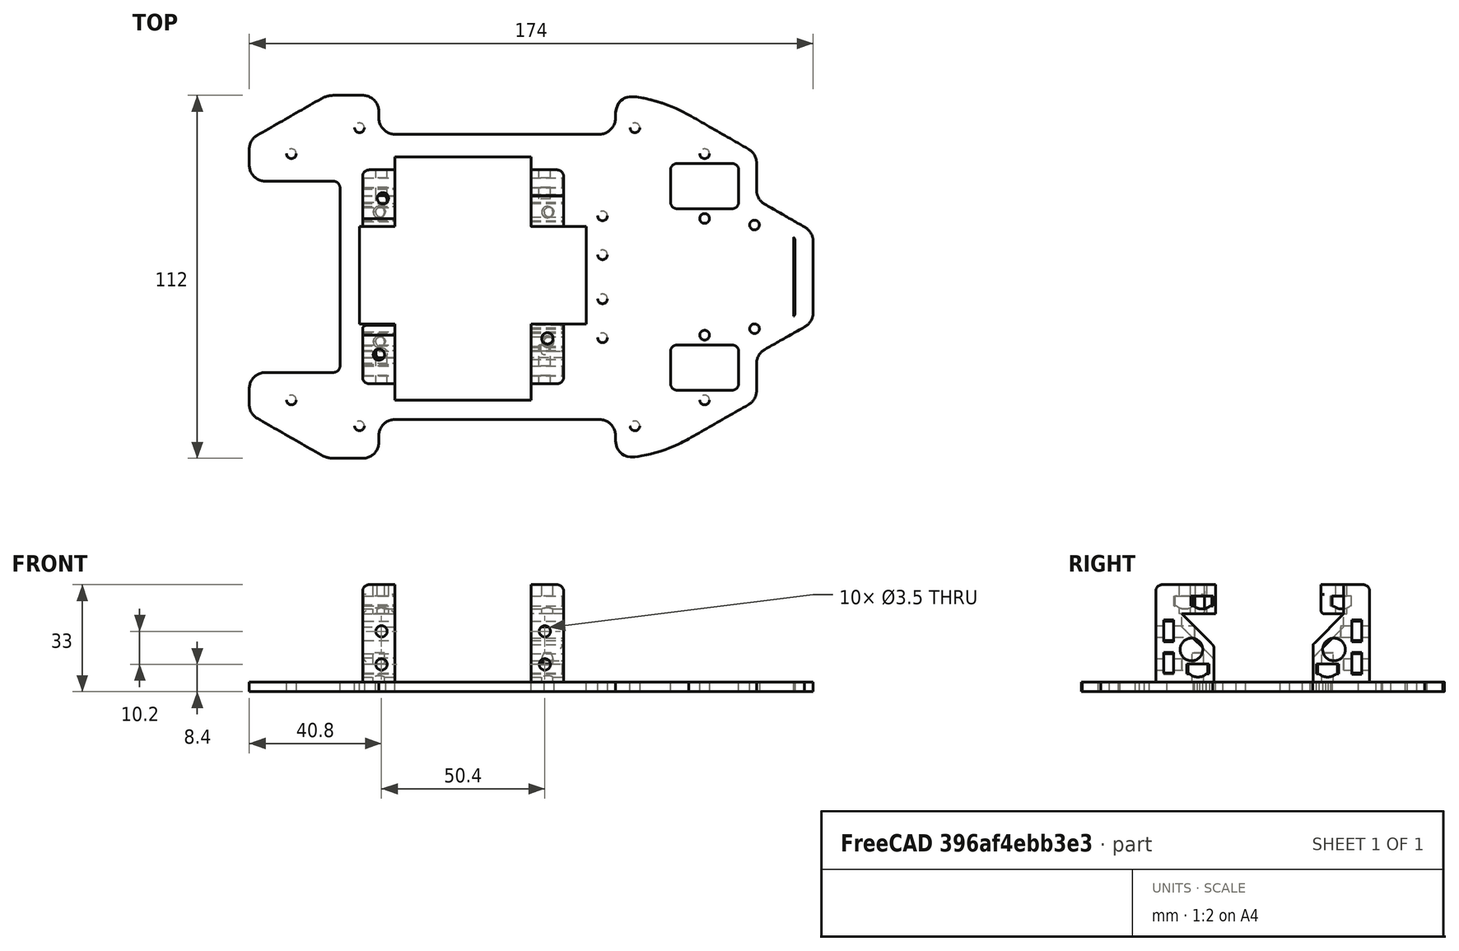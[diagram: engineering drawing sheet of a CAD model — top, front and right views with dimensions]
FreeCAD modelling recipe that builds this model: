
FCSTD DOCUMENT  (FreeCAD 0.16R6692 (Git))
Label: Base y cuerpo cortados
License: All rights reserved
LicenseURL: http://es.wikipedia.org/wiki/Todos_los_derechos_reservados
objects: Part::Box×7, Part::Cut×6, Part::Feature×2, Part::Fillet×1, Part::Chamfer×1, Part::MultiFuse×1, Part::FeaturePython×1
note: 19 computed .brp shape members not serialized (recipe doc carries the construction recipe); baked Part::Feature solids carry a one-line shape summary decoded from their .brp

FEATURE [Part::Feature] Cut048016001  label="Cut048017"
  shape: bbox 62 x 66 x 30 mm, 214 faces (baked)
FEATURE [Part::Fillet] Fillet  label="Redondeo_cuerpo"
  Base = -> Cut048016001
  Edges = 35 edges: [Edge159 r=1,Edge162 r=2,Edge164 r=2,Edge166 r=2,Edge169 r=2,Edge170 r=2,Edge171 r=2,Edge172 r=1,Edge173 r=1,Edge174 r=1,Edge175 r=1,Edge180 r=2,Edge183 r=2,Edge191 r=1,Edge192 r=1,Edge193 r=1,Edge195 r=1,Edge197 r=1,Edge204 r=1,Edge206 r=1,Edge272 r=1,Edge273 r=1,Edge274 r=1,Edge275 r=1,Edge276 r=1,Edge294 r=1,Edge295 r=1,Edge391 r=2,Edge393 r=1,Edge397 r=2,Edge403 r=1,Edge523 r=2,Edge525 r=1,Edge549 r=2,Edge550 r=1]
FEATURE [Part::Chamfer] Chamfer009  label="CUERPO_FINAL"
  Base = -> Fillet
  Edges = 30 edges r=0.4: [Edge70,Edge72,Edge74,Edge79,Edge89,Edge92,Edge96,Edge99,Edge101,Edge102,Edge104,Edge106,Edge108,Edge110,Edge112,Edge419,Edge421,Edge424,Edge426,Edge430,Edge432,Edge436,Edge438,Edge441,Edge443,Edge444,Edge446,Edge448,Edge450,Edge455]
FEATURE [Part::Feature] Part__Feature210  label="BASE_FINAL"
  shape: bbox 217.5 x 140 x 48.35 mm, 110 faces (baked)
FEATURE [Part::Box] Box  label="Cubo Y corte base"
  Height = 46
  Length = 42
  Placement = pos=(-12,-38,0) rot=(0,0,1;0rad)
  Width = 75
FEATURE [Part::Box] Box003  label="Cubo X corte cuerpo"
  Height = 49
  Length = 70
  Placement = pos=(-23,-14.5,0) rot=(0,0,1;0rad)
  Width = 30
FEATURE [Part::Box] Box004  label="Cubo Y corte Cuerpo"
  Height = 46
  Length = 42
  Placement = pos=(-12,-38,0) rot=(0,0,1;0rad)
  Width = 75
FEATURE [Part::Box] Box005  label="Cubo X corte base"
  Height = 49
  Length = 70
  Placement = pos=(-23,-14.5,0) rot=(0,0,1;0rad)
  Width = 30
FEATURE [Part::Cut] Cut  label="base"
  Base = -> Part__Feature210
  Tool = -> Box005
FEATURE [Part::Cut] Cut048016002  label="Base Cortada"
  Base = -> Cut
  Tool = -> Box
FEATURE [Part::Cut] Cut048016003
  Base = -> Chamfer009
  Tool = -> Box003
FEATURE [Part::Cut] Cut048016004  label="Cuerpo Cortado"
  Base = -> Cut048016003
  Tool = -> Box004
FEATURE [Part::MultiFuse] Fusion
  Shapes = -> [Cut048016004,Cut048016002]
FEATURE [Part::Box] Box006  label="Cubo X corte cuerpo001"
  Height = 6
  Length = 45
  Placement = pos=(-23,-18,28) rot=(0,0,1;0rad)
  Width = 36
FEATURE [Part::Cut] Cut048016005
  Base = -> Fusion
  Tool = -> Box006
FEATURE [Part::Box] Box007  label="Cubo X corte cuerpo002"
  Height = 6
  Length = 45
  Placement = pos=(4,-11,28) rot=(0,0,1;0rad)
  Width = 36
FEATURE [Part::Cut] Cut048016006  label="BaseCuerpoCortados"
  Base = -> Cut048016005
  Tool = -> Box007
FEATURE [Part::Box] Box008  label="Cubo"
  Height = 3
  Length = 30
  Placement = pos=(81,-17,0) rot=(0,0,1;0rad)
  Width = 34
FEATURE [Part::FeaturePython] Connect  # WARN: FeaturePython — macro-defined, semantics opaque (R4)
  Base = -> Cut048016006
  Mode = 1
  Placement = pos=(-1,3,1) rot=(0,0,1;0rad)
  Refine = true
  Tool = -> Box008
